# Revit family: Electronics_Community-Point-Source_Biamp_Loudspeaker_R_5
name_source: partatom
category: Communication Devices
units: mm (PartAtom-declared; Revit-internal decimal feet)

## family parameters
Cut with Voids When Loaded = No
Host = Face
Maintain Annotation Orientation = No
OmniClass Number = 23.85.10.11.14.14.14
OmniClass Title = Loudspeakers
Part Type = Normal
Room Calculation Point = No
Round Connector Dimension = Use Diameter
Shared = No

## types (6) — shared parameters
Crossover Frequency = 2 kHz
Default Elevation = 48 "
Depth = 15.94 "
Description = R.5 2-Way Horn Loaded Weather-Resistant Full-Range Loudspeaker
Driver Protection = DYNA-TECH
Drivers = LF (1) 12 Ferrofluid-cooled HF (1) 1 exit, titanium free, Ferrofluid-cooled
Enclosure = Rotomolded LLDPE, light grey
Environmental = IEC529 IP55W rating with a minimum 5-degree downward aiming angle
Grill Material = Biamp - Plastic - Gray(Grid)
Grille = 3-layer WeatherStop™, light grey (Zinc-rich epoxy dual-layer powder coated perforated steel grille, foam, woven poly mesh)
Height = 16 "
Housing Material = Biamp - Plastic - Gray
Input Connection = 12 foot (4 m) SJOW #16 gauge
Loudspeaker Type = 2-way, horn loaded coaxial, weather-resistant
Manufacturer = Biamp
Mounting/Rigging Provisions = (5) 3/8-16 rigging points
Product Documentation Link = https://downloads.biamp.com
Product Page URL = https://www.biamp.com
Product data url = https://www.bimobject.com
Recommended Signal Processing = 90 Hz high pass filter
Required Accessories = 24 dB/Oct high pass filter
URL = https://www.biamp.com
Width = 16 "
Yoke Material = Biamp - Metal - Gray

## per-type parameters (varying)
| type | 200W Minimum Impedance | 200W Nominal Impedance | Axial Q / DI | Connector Description | Controls | Max Input Ratings | Maximum Output | Maximum Output on 200W Tap | Minimum Impedance | Nominal Impedance | Nominal –6dB Beamwidth | Operating Range | Recommended Power Amplifier | Sensitivity (1W/1m) | Weight |
| R.5-66Z |  |  | 21.4  / 13.3, 1.6 kHz to 12.5 kHz | Terminal strip; 200W continuous, 500W program, 40 volts RMS, 89 volts momentary peak | None | 200W continuous, 500W program 40 volts RMS, 89 volts momentary peak | 126 dB SPL / 133 dB SPL (peak) | 125 dB SPL | 4.1 ohms @ 9.6 kHz | 8 ohms | 60° H (+3° / -8°, 1.6 kHz to 12.5 kHz) 60° V (+20° / -16°, 1.6 kHz to 12.5 kHz) | 85 Hz to 16 kHz 125 Hz to 10 kHz (±4 dB) | 420W to 600W @ 8 ohms | 102 dB SPL (125 Hz to 10 kHz 1/3 octave bands) 102 dB SPL (250 Hz to 4 kHz speech range) | 15.90 kgf |
| R.5-66TZ | 16.4 ohms @ 9.3 kHz | 25 ohms | 21.4  / 13.3, 1.6 kHz to 12.5 kHz | Terminal strip; 70V/100V operation | 4 position autoformer TAP select switch;70V switchable taps @ 200W, 100W, 50W, 25W;100V switchable taps @ 200W, 100W, 50W | 200W, 70V/100V |  | 125 dB SPL |  |  | 60° H (+3° / -8°, 1.6 kHz to 12.5 kHz) 60° V (+20° / -16°, 1.6 kHz to 12.5 kHz) | 85 Hz to 16 kHz 125 Hz to 10 kHz (±4 dB) | 25W to 200W @ 70 Volts; 50W to 200W @ 100 Volts | 102 dB SPL (125 Hz to 10 kHz 1/3 octave bands) 102 dB SPL (250 Hz to 4 kHz speech range) | 16.80 kgf |
| R.5-94Z |  |  | 18.1  / 12.6, 1.6 kHz to 10 kHz | Terminal strip; 200W continuous, 500W program, 40 volts RMS, 89 volts momentary peak | None | 200W continuous, 500W program 40 volts RMS, 89 volts momentary peak | 124 dB SPL / 131 dB SPL (peak) | 125 dB SPL | 4.2 ohms @ 9.7 kHz | 8 ohms | 90° H (+1° / -46°, 1.6 kHz to 12.5 kHz); 40° V (+16° / +1°, 1.6 kHz to 12.5 kHz) | 85 Hz to 16 kHz 125 Hz to 10 kHz (±4 dB) | 420W to 600W @ 8 ohms | 101 dB SPL (125 Hz to 10 kHz 1/3 octave bands) 102 dB SPL (250 Hz to 4 kHz speech range) | 15.90 kgf |
| R.5-94TZ | 16.4 ohms @ 8.7 kHz | 25 ohms | 18.1  / 12.6, 1.6 kHz to 10 kHz | Terminal strip; 70V/100V operation | 4 position autoformer TAP select switch;70V switchable taps @ 200W, 100W, 50W, 25W;100V switchable taps @ 200W, 100W, 50W | 200W, 70V/100V |  | 123 dB SPL |  |  | 90° H (+1° / -46°, 1.6 kHz to 12.5 kHz); 40° V (+16° / +1°, 1.6 kHz to 12.5 kHz) | 85 Hz to 16 kHz 125 Hz to 10 kHz (±4 dB) | 25W to 200W @ 70 Volts; 50W to 200W @ 100 Volts | 100 dB SPL (125 Hz to 10 kHz 1/3 octave bands) 101 dB SPL (250 Hz to 4 kHz speech range) | 16.80 kgf |
| R.5-99Z |  |  | 13.6  / 11.3, 1.6 kHz to 10 kHz | Terminal strip; 200W continuous, 500W program, 40 volts RMS, 89 volts momentary peak | None | 200W continuous, 500W program 40 volts RMS, 89 volts momentary peak | 124 dB SPL / 131 dB SPL (peak) | 125 dB SPL | 4.2 ohms @ 9.5 kH | 8 ohms | 90° H (+2° / -43°, 1.6 kHz to 12.5 kHz); 90° V (+6° / -46°, 1.6 kHz to 12.5 kHz) | 85 Hz to 16 kHz 125 Hz to 10 kHz (±5 dB) | 420W to 600W @ 8 ohms | 101 dB SPL (125 Hz to 10 kHz 1/3 octave bands) 101 dB SPL (250 Hz to 4 kHz speech range) | 15.90 kgf |
| R.5-99TZ | 16.2 ohms @ 8.6 kHz | 25 ohms | 13.6  / 11.3, 1.6 kHz to 10 kHz | Terminal strip; 70V/100V operation | 4 position autoformer TAP select switch;70V switchable taps @ 200W, 100W, 50W, 25W;100V switchable taps @ 200W, 100W, 50W | 200W, 70V/100V |  | 123 dB SPL |  |  | 90° H (+2° / -43°, 1.6 kHz to 12.5 kHz); 90° V (+6° / -46°, 1.6 kHz to 12.5 kHz) | 85 Hz to 16 kHz 125 Hz to 10 kHz (±4 dB) | 25W to 200W @ 70 Volts; 50W to 200W @ 100 Volts | 100 dB SPL (125 Hz to 10 kHz 1/3 octave bands) 100 dB SPL (250 Hz to 4 kHz speech range) | 16.80 kgf |

note: column(s) folded — value = type name in every type: Model

## geometry (parser evidence)
native form markers: Sweep x4
no freeform markers — native parametric forms only
